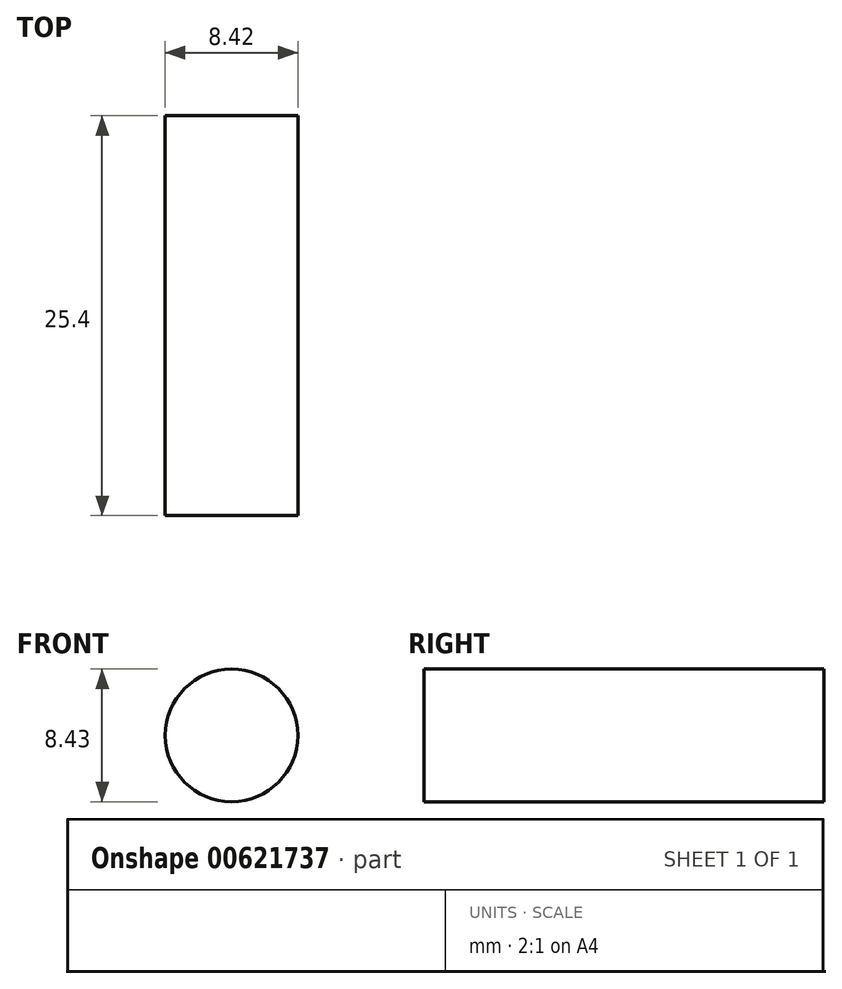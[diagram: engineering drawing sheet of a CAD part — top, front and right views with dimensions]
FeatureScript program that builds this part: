
annotation { "Feature Type Name" : "Feature", "Feature Type Description" : "" }
export const myFeature = defineFeature(function(context is Context, id is Id, definition is map)
    precondition{}
    {
        {
            var Q0;
            Q0=qCreatedBy(makeId("Front.planeOp"),FACE);
            var sketch = newSketch(context, id + "F0", { "sketchPlane" : qUnion([Q0])});
            skLineSegment(sketch, "E0.bottom", {"start": v(-11.28, -4.9) * mm, "end": v(21.6, -4.9) * mm});
            skLineSegment(sketch, "E0.top", {"start": v(-11.28, 13.12) * mm, "end": v(21.6, 13.12) * mm});
            skLineSegment(sketch, "E0.left", {"start": v(-11.28, -4.9) * mm, "end": v(-11.28, 13.12) * mm});
            skLineSegment(sketch, "E0.right", {"start": v(21.6, -4.9) * mm, "end": v(21.6, 13.12) * mm});
            skCircle(sketch, "E1", {"center": v(10.23, 7.35) * mm, "radius": 4.21 * mm});
            skSolve(sketch);
        }
        {
            var Q0;
            Q0=makeQuery(id+"F0.imprint","IMPRINT",FACE,{"disambiguationData":[TD([[makeQuery(id+"F0.imprint","IMPRINT",EDGE,{"derivedFrom":sQuery(id+"F0.wireOp",EDGE,"E1")}),1.0]])]});
            extrude(context, id + "F1", {"entities" : qUnion([Q0]), "depth" : 25.4 * mm, "offsetDistance" : 25.4 * mm});
        }
    });
